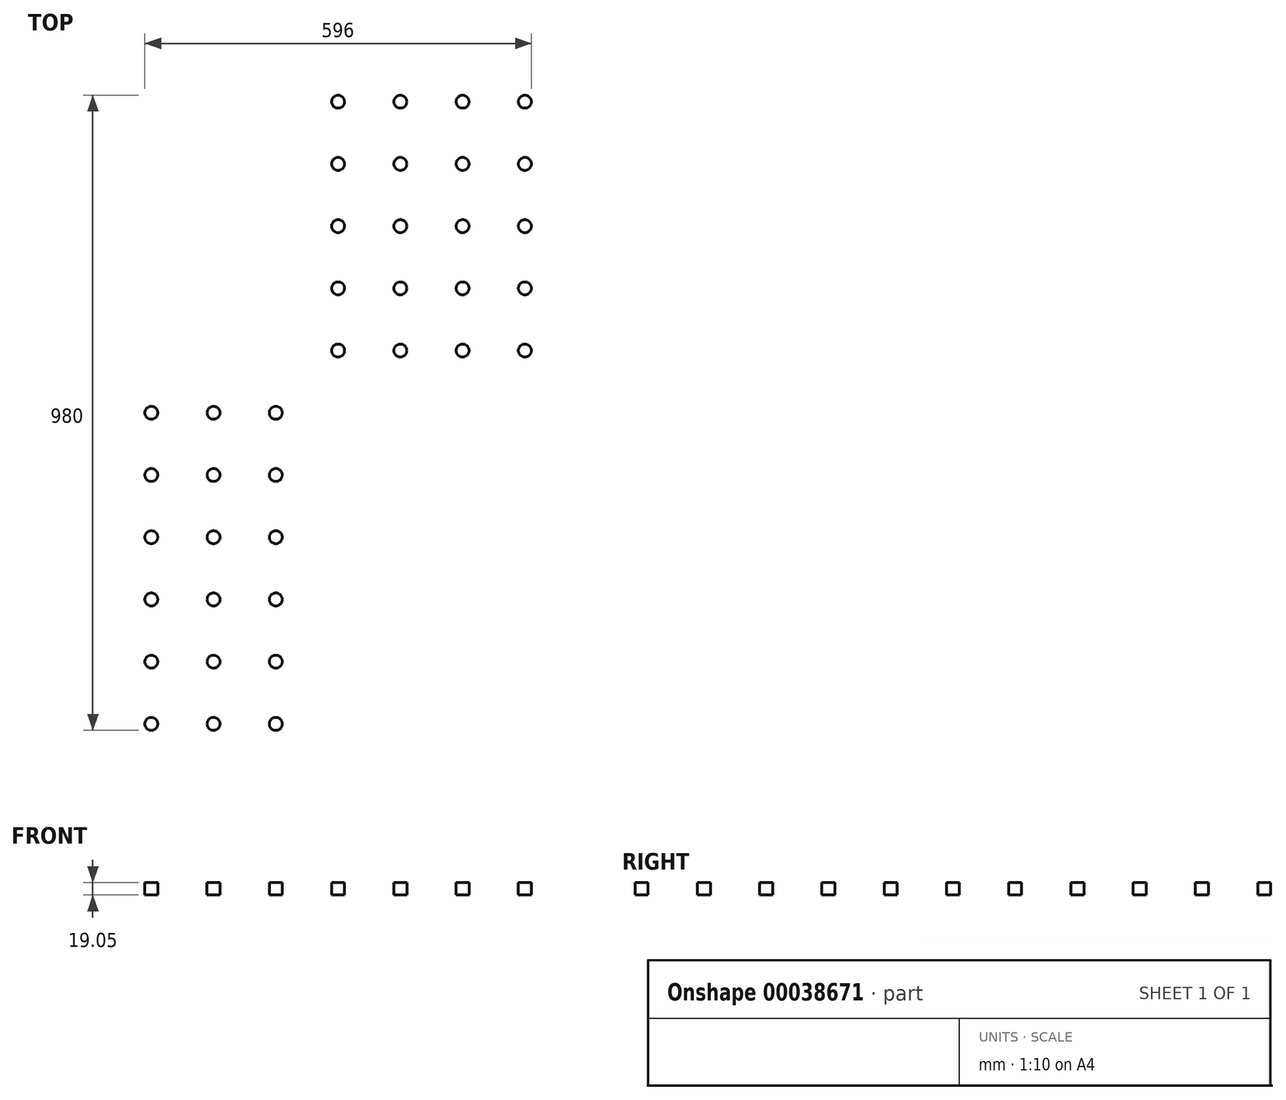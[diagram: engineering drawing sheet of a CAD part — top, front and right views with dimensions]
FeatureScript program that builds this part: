
annotation { "Feature Type Name" : "Feature", "Feature Type Description" : "" }
export const myFeature = defineFeature(function(context is Context, id is Id, definition is map)
    precondition{}
    {
        {
            var Q0;
            Q0=qCreatedBy(makeId("Top.planeOp"),FACE);
            var sketch = newSketch(context, id + "F0", { "sketchPlane" : qUnion([Q0])});
            skLineSegment(sketch, "E0.bottom", {"start": v(0, 0) * mm, "end": v(718, 0) * mm});
            skLineSegment(sketch, "E0.top", {"start": v(0, -1102) * mm, "end": v(718, -1102) * mm});
            skLineSegment(sketch, "E0.left", {"start": v(0, 0) * mm, "end": v(0, -1102) * mm});
            skLineSegment(sketch, "E0.right", {"start": v(718, 0) * mm, "end": v(718, -1102) * mm});
            skSolve(sketch);
        }
        {
            var Q0;
            Q0=makeQuery(id+"F0.imprint","IMPRINT",FACE,{"disambiguationData":[TD([[makeQuery(id+"F0.imprint","IMPRINT",EDGE,{"derivedFrom":sQuery(id+"F0.wireOp",EDGE,"E0.bottom")}),-1.0]])]});
            extrude(context, id + "F1", {"entities" : qUnion([Q0]), "oppositeDirection" : true, "depth" : 19.05 * mm});
        }
        {
            var Q0;
            Q0=makeQuery(id+"F1.opExtrude","CAP_FACE",FACE,{"disambiguationData":[OSD([sQuery(id+"F0.wireOp",EDGE,"E0.bottom"),sQuery(id+"F0.wireOp",EDGE,"E0.top"),sQuery(id+"F0.wireOp",EDGE,"E0.left"),sQuery(id+"F0.wireOp",EDGE,"E0.right")])],"isStart":false});
            var sketch = newSketch(context, id + "F2", { "sketchPlane" : qUnion([Q0])});
            skLineSegment(sketch, "E1", {"start": v(0, 551) * mm, "end": v(718, 551) * mm, "construction": true});
            skLineSegment(sketch, "E2", {"start": v(359, 1102) * mm, "end": v(359, 0) * mm, "construction": true});
            skCircle(sketch, "E3", {"center": v(359, 551) * mm, "radius": 10 * mm});
            skCircle(sketch, "E4.0.1.0", {"center": v(359, 647) * mm, "radius": 10 * mm});
            skCircle(sketch, "E4.0.2.0", {"center": v(359, 743) * mm, "radius": 10 * mm});
            skCircle(sketch, "E4.0.3.0", {"center": v(359, 839) * mm, "radius": 10 * mm});
            skCircle(sketch, "E4.0.4.0", {"center": v(359, 935) * mm, "radius": 10 * mm});
            skCircle(sketch, "E4.0.5.0", {"center": v(359, 1031) * mm, "radius": 10 * mm});
            skCircle(sketch, "E4.1.0.0", {"center": v(455, 551) * mm, "radius": 10 * mm});
            skCircle(sketch, "E4.1.1.0", {"center": v(455, 647) * mm, "radius": 10 * mm});
            skCircle(sketch, "E4.1.2.0", {"center": v(455, 743) * mm, "radius": 10 * mm});
            skCircle(sketch, "E4.1.3.0", {"center": v(455, 839) * mm, "radius": 10 * mm});
            skCircle(sketch, "E4.1.4.0", {"center": v(455, 935) * mm, "radius": 10 * mm});
            skCircle(sketch, "E4.1.5.0", {"center": v(455, 1031) * mm, "radius": 10 * mm});
            skCircle(sketch, "E4.2.0.0", {"center": v(551, 551) * mm, "radius": 10 * mm});
            skCircle(sketch, "E4.2.1.0", {"center": v(551, 647) * mm, "radius": 10 * mm});
            skCircle(sketch, "E4.2.2.0", {"center": v(551, 743) * mm, "radius": 10 * mm});
            skCircle(sketch, "E4.2.3.0", {"center": v(551, 839) * mm, "radius": 10 * mm});
            skCircle(sketch, "E4.2.4.0", {"center": v(551, 935) * mm, "radius": 10 * mm});
            skCircle(sketch, "E4.2.5.0", {"center": v(551, 1031) * mm, "radius": 10 * mm});
            skCircle(sketch, "E4.3.0.0", {"center": v(647, 551) * mm, "radius": 10 * mm});
            skCircle(sketch, "E4.3.1.0", {"center": v(647, 647) * mm, "radius": 10 * mm});
            skCircle(sketch, "E4.3.2.0", {"center": v(647, 743) * mm, "radius": 10 * mm});
            skCircle(sketch, "E4.3.3.0", {"center": v(647, 839) * mm, "radius": 10 * mm});
            skCircle(sketch, "E4.3.4.0", {"center": v(647, 935) * mm, "radius": 10 * mm});
            skCircle(sketch, "E4.3.5.0", {"center": v(647, 1031) * mm, "radius": 10 * mm});
            skLineSegment(sketch, "E4.direction1", {"start": v(359, 551) * mm, "end": v(455, 551) * mm, "construction": true});
            skLineSegment(sketch, "E4.direction2", {"start": v(359, 551) * mm, "end": v(359, 647) * mm, "construction": true});
            skCircle(sketch, "E5.MirrorC", {"center": v(263, 551) * mm, "radius": 10 * mm});
            skCircle(sketch, "E6.MirrorC", {"center": v(263, 839) * mm, "radius": 10 * mm});
            skCircle(sketch, "E7.MirrorC", {"center": v(167, 551) * mm, "radius": 10 * mm});
            skCircle(sketch, "E8.MirrorC", {"center": v(71, 1031) * mm, "radius": 10 * mm});
            skCircle(sketch, "E9.MirrorC", {"center": v(71, 839) * mm, "radius": 10 * mm});
            skCircle(sketch, "E10.MirrorC", {"center": v(71, 743) * mm, "radius": 10 * mm});
            skCircle(sketch, "E11.MirrorC", {"center": v(71, 935) * mm, "radius": 10 * mm});
            skCircle(sketch, "E12.MirrorC", {"center": v(71, 647) * mm, "radius": 10 * mm});
            skCircle(sketch, "E13.MirrorC", {"center": v(167, 839) * mm, "radius": 10 * mm});
            skCircle(sketch, "E14.MirrorC", {"center": v(167, 935) * mm, "radius": 10 * mm});
            skCircle(sketch, "E15.MirrorC", {"center": v(167, 1031) * mm, "radius": 10 * mm});
            skCircle(sketch, "E16.MirrorC", {"center": v(167, 647) * mm, "radius": 10 * mm});
            skCircle(sketch, "E17.MirrorC", {"center": v(71, 551) * mm, "radius": 10 * mm});
            skCircle(sketch, "E18.MirrorC", {"center": v(167, 743) * mm, "radius": 10 * mm});
            skCircle(sketch, "E19.MirrorC", {"center": v(263, 935) * mm, "radius": 10 * mm});
            skCircle(sketch, "E20.MirrorC", {"center": v(263, 647) * mm, "radius": 10 * mm});
            skCircle(sketch, "E21.MirrorC", {"center": v(263, 1031) * mm, "radius": 10 * mm});
            skCircle(sketch, "E22.MirrorC", {"center": v(263, 743) * mm, "radius": 10 * mm});
            skCircle(sketch, "E23.MirrorC", {"center": v(263, 359) * mm, "radius": 10 * mm});
            skCircle(sketch, "E24.MirrorC", {"center": v(359, 455) * mm, "radius": 10 * mm});
            skCircle(sketch, "E25.MirrorC", {"center": v(551, 71) * mm, "radius": 10 * mm});
            skCircle(sketch, "E26.MirrorC", {"center": v(455, 455) * mm, "radius": 10 * mm});
            skCircle(sketch, "E27.MirrorC", {"center": v(359, 263) * mm, "radius": 10 * mm});
            skCircle(sketch, "E28.MirrorC", {"center": v(359, 359) * mm, "radius": 10 * mm});
            skCircle(sketch, "E29.MirrorC", {"center": v(551, 359) * mm, "radius": 10 * mm});
            skCircle(sketch, "E30.MirrorC", {"center": v(71, 263) * mm, "radius": 10 * mm});
            skCircle(sketch, "E31.MirrorC", {"center": v(551, 263) * mm, "radius": 10 * mm});
            skCircle(sketch, "E32.MirrorC", {"center": v(167, 263) * mm, "radius": 10 * mm});
            skCircle(sketch, "E33.MirrorC", {"center": v(263, 263) * mm, "radius": 10 * mm});
            skCircle(sketch, "E34.MirrorC", {"center": v(647, 263) * mm, "radius": 10 * mm});
            skCircle(sketch, "E35.MirrorC", {"center": v(167, 455) * mm, "radius": 10 * mm});
            skCircle(sketch, "E36.MirrorC", {"center": v(263, 455) * mm, "radius": 10 * mm});
            skCircle(sketch, "E37.MirrorC", {"center": v(455, 359) * mm, "radius": 10 * mm});
            skCircle(sketch, "E38.MirrorC", {"center": v(455, 263) * mm, "radius": 10 * mm});
            skCircle(sketch, "E39.MirrorC", {"center": v(71, 359) * mm, "radius": 10 * mm});
            skCircle(sketch, "E40.MirrorC", {"center": v(455, 71) * mm, "radius": 10 * mm});
            skCircle(sketch, "E41.MirrorC", {"center": v(647, 359) * mm, "radius": 10 * mm});
            skCircle(sketch, "E42.MirrorC", {"center": v(167, 71) * mm, "radius": 10 * mm});
            skCircle(sketch, "E43.MirrorC", {"center": v(359, 71) * mm, "radius": 10 * mm});
            skCircle(sketch, "E44.MirrorC", {"center": v(71, 71) * mm, "radius": 10 * mm});
            skCircle(sketch, "E45.MirrorC", {"center": v(359, 167) * mm, "radius": 10 * mm});
            skCircle(sketch, "E46.MirrorC", {"center": v(167, 167) * mm, "radius": 10 * mm});
            skCircle(sketch, "E47.MirrorC", {"center": v(263, 71) * mm, "radius": 10 * mm});
            skCircle(sketch, "E48.MirrorC", {"center": v(71, 455) * mm, "radius": 10 * mm});
            skCircle(sketch, "E49.MirrorC", {"center": v(551, 167) * mm, "radius": 10 * mm});
            skCircle(sketch, "E50.MirrorC", {"center": v(167, 359) * mm, "radius": 10 * mm});
            skCircle(sketch, "E51.MirrorC", {"center": v(647, 71) * mm, "radius": 10 * mm});
            skCircle(sketch, "E52.MirrorC", {"center": v(551, 455) * mm, "radius": 10 * mm});
            skCircle(sketch, "E53.MirrorC", {"center": v(647, 167) * mm, "radius": 10 * mm});
            skCircle(sketch, "E54.MirrorC", {"center": v(455, 167) * mm, "radius": 10 * mm});
            skCircle(sketch, "E55.MirrorC", {"center": v(263, 167) * mm, "radius": 10 * mm});
            skCircle(sketch, "E56.MirrorC", {"center": v(647, 455) * mm, "radius": 10 * mm});
            skCircle(sketch, "E57.MirrorC", {"center": v(71, 167) * mm, "radius": 10 * mm});
            skSolve(sketch);
        }
        {
            var Q0;
            Q0=makeQuery(id+"F2.imprint","IMPRINT",FACE,{"disambiguationData":[TD([[makeQuery(id+"F2.imprint","IMPRINT",EDGE,{"derivedFrom":sQuery(id+"F2.wireOp",EDGE,"E3")}),1.0]])]});
            var Q1;
            Q1=makeQuery(id+"F2.imprint","IMPRINT",FACE,{"disambiguationData":[TD([[makeQuery(id+"F2.imprint","IMPRINT",EDGE,{"derivedFrom":sQuery(id+"F2.wireOp",EDGE,"E5.MirrorC")}),-1.0]])]});
            var Q2;
            Q2=makeQuery(id+"F2.imprint","IMPRINT",FACE,{"disambiguationData":[TD([[makeQuery(id+"F2.imprint","IMPRINT",EDGE,{"derivedFrom":sQuery(id+"F2.wireOp",EDGE,"E4.3.4.0")}),1.0]])]});
            var Q3;
            Q3=makeQuery(id+"F2.imprint","IMPRINT",FACE,{"disambiguationData":[TD([[makeQuery(id+"F2.imprint","IMPRINT",EDGE,{"derivedFrom":sQuery(id+"F2.wireOp",EDGE,"E19.MirrorC")}),-1.0]])]});
            var Q4;
            Q4=makeQuery(id+"F2.imprint","IMPRINT",FACE,{"disambiguationData":[TD([[makeQuery(id+"F2.imprint","IMPRINT",EDGE,{"derivedFrom":sQuery(id+"F2.wireOp",EDGE,"E27.MirrorC")}),-1.0]])]});
            var Q5;
            Q5=makeQuery(id+"F2.imprint","IMPRINT",FACE,{"disambiguationData":[TD([[makeQuery(id+"F2.imprint","IMPRINT",EDGE,{"derivedFrom":sQuery(id+"F2.wireOp",EDGE,"E30.MirrorC")}),1.0]])]});
            var Q6;
            Q6=makeQuery(id+"F2.imprint","IMPRINT",FACE,{"disambiguationData":[TD([[makeQuery(id+"F2.imprint","IMPRINT",EDGE,{"derivedFrom":sQuery(id+"F2.wireOp",EDGE,"E4.2.5.0")}),1.0]])]});
            var Q7;
            Q7=makeQuery(id+"F2.imprint","IMPRINT",FACE,{"disambiguationData":[TD([[makeQuery(id+"F2.imprint","IMPRINT",EDGE,{"derivedFrom":sQuery(id+"F2.wireOp",EDGE,"E53.MirrorC")}),-1.0]])]});
            var Q8;
            Q8=makeQuery(id+"F2.imprint","IMPRINT",FACE,{"disambiguationData":[TD([[makeQuery(id+"F2.imprint","IMPRINT",EDGE,{"derivedFrom":sQuery(id+"F2.wireOp",EDGE,"E22.MirrorC")}),-1.0]])]});
            var Q9;
            Q9=makeQuery(id+"F2.imprint","IMPRINT",FACE,{"disambiguationData":[TD([[makeQuery(id+"F2.imprint","IMPRINT",EDGE,{"derivedFrom":sQuery(id+"F2.wireOp",EDGE,"E44.MirrorC")}),1.0]])]});
            var Q10;
            Q10=makeQuery(id+"F2.imprint","IMPRINT",FACE,{"disambiguationData":[TD([[makeQuery(id+"F2.imprint","IMPRINT",EDGE,{"derivedFrom":sQuery(id+"F2.wireOp",EDGE,"E37.MirrorC")}),-1.0]])]});
            var Q11;
            Q11=makeQuery(id+"F2.imprint","IMPRINT",FACE,{"disambiguationData":[TD([[makeQuery(id+"F2.imprint","IMPRINT",EDGE,{"derivedFrom":sQuery(id+"F2.wireOp",EDGE,"E34.MirrorC")}),-1.0]])]});
            var Q12;
            Q12=makeQuery(id+"F2.imprint","IMPRINT",FACE,{"disambiguationData":[TD([[makeQuery(id+"F2.imprint","IMPRINT",EDGE,{"derivedFrom":sQuery(id+"F2.wireOp",EDGE,"E6.MirrorC")}),-1.0]])]});
            var Q13;
            Q13=makeQuery(id+"F2.imprint","IMPRINT",FACE,{"disambiguationData":[TD([[makeQuery(id+"F2.imprint","IMPRINT",EDGE,{"derivedFrom":sQuery(id+"F2.wireOp",EDGE,"E43.MirrorC")}),-1.0]])]});
            var Q14;
            Q14=makeQuery(id+"F2.imprint","IMPRINT",FACE,{"disambiguationData":[TD([[makeQuery(id+"F2.imprint","IMPRINT",EDGE,{"derivedFrom":sQuery(id+"F2.wireOp",EDGE,"E39.MirrorC")}),1.0]])]});
            var Q15;
            Q15=makeQuery(id+"F2.imprint","IMPRINT",FACE,{"disambiguationData":[TD([[makeQuery(id+"F2.imprint","IMPRINT",EDGE,{"derivedFrom":sQuery(id+"F2.wireOp",EDGE,"E55.MirrorC")}),1.0]])]});
            var Q16;
            Q16=makeQuery(id+"F2.imprint","IMPRINT",FACE,{"disambiguationData":[TD([[makeQuery(id+"F2.imprint","IMPRINT",EDGE,{"derivedFrom":sQuery(id+"F2.wireOp",EDGE,"E56.MirrorC")}),-1.0]])]});
            var Q17;
            Q17=makeQuery(id+"F2.imprint","IMPRINT",FACE,{"disambiguationData":[TD([[makeQuery(id+"F2.imprint","IMPRINT",EDGE,{"derivedFrom":sQuery(id+"F2.wireOp",EDGE,"E40.MirrorC")}),-1.0]])]});
            var Q18;
            Q18=makeQuery(id+"F2.imprint","IMPRINT",FACE,{"disambiguationData":[TD([[makeQuery(id+"F2.imprint","IMPRINT",EDGE,{"derivedFrom":sQuery(id+"F2.wireOp",EDGE,"E4.1.5.0")}),1.0]])]});
            var Q19;
            Q19=makeQuery(id+"F2.imprint","IMPRINT",FACE,{"disambiguationData":[TD([[makeQuery(id+"F2.imprint","IMPRINT",EDGE,{"derivedFrom":sQuery(id+"F2.wireOp",EDGE,"E54.MirrorC")}),-1.0]])]});
            var Q20;
            Q20=makeQuery(id+"F2.imprint","IMPRINT",FACE,{"disambiguationData":[TD([[makeQuery(id+"F2.imprint","IMPRINT",EDGE,{"derivedFrom":sQuery(id+"F2.wireOp",EDGE,"E28.MirrorC")}),-1.0]])]});
            var Q21;
            Q21=makeQuery(id+"F2.imprint","IMPRINT",FACE,{"disambiguationData":[TD([[makeQuery(id+"F2.imprint","IMPRINT",EDGE,{"derivedFrom":sQuery(id+"F2.wireOp",EDGE,"E32.MirrorC")}),1.0]])]});
            var Q22;
            Q22=makeQuery(id+"F2.imprint","IMPRINT",FACE,{"disambiguationData":[TD([[makeQuery(id+"F2.imprint","IMPRINT",EDGE,{"derivedFrom":sQuery(id+"F2.wireOp",EDGE,"E50.MirrorC")}),1.0]])]});
            var Q23;
            Q23=makeQuery(id+"F2.imprint","IMPRINT",FACE,{"disambiguationData":[TD([[makeQuery(id+"F2.imprint","IMPRINT",EDGE,{"derivedFrom":sQuery(id+"F2.wireOp",EDGE,"E12.MirrorC")}),-1.0]])]});
            var Q24;
            Q24=makeQuery(id+"F2.imprint","IMPRINT",FACE,{"disambiguationData":[TD([[makeQuery(id+"F2.imprint","IMPRINT",EDGE,{"derivedFrom":sQuery(id+"F2.wireOp",EDGE,"E24.MirrorC")}),-1.0]])]});
            var Q25;
            Q25=makeQuery(id+"F2.imprint","IMPRINT",FACE,{"disambiguationData":[TD([[makeQuery(id+"F2.imprint","IMPRINT",EDGE,{"derivedFrom":sQuery(id+"F2.wireOp",EDGE,"E4.2.3.0")}),1.0]])]});
            var Q26;
            Q26=makeQuery(id+"F2.imprint","IMPRINT",FACE,{"disambiguationData":[TD([[makeQuery(id+"F2.imprint","IMPRINT",EDGE,{"derivedFrom":sQuery(id+"F2.wireOp",EDGE,"E38.MirrorC")}),-1.0]])]});
            var Q27;
            Q27=makeQuery(id+"F2.imprint","IMPRINT",FACE,{"disambiguationData":[TD([[makeQuery(id+"F2.imprint","IMPRINT",EDGE,{"derivedFrom":sQuery(id+"F2.wireOp",EDGE,"E4.3.3.0")}),1.0]])]});
            var Q28;
            Q28=makeQuery(id+"F2.imprint","IMPRINT",FACE,{"disambiguationData":[TD([[makeQuery(id+"F2.imprint","IMPRINT",EDGE,{"derivedFrom":sQuery(id+"F2.wireOp",EDGE,"E14.MirrorC")}),-1.0]])]});
            var Q29;
            Q29=makeQuery(id+"F2.imprint","IMPRINT",FACE,{"disambiguationData":[TD([[makeQuery(id+"F2.imprint","IMPRINT",EDGE,{"derivedFrom":sQuery(id+"F2.wireOp",EDGE,"E21.MirrorC")}),-1.0]])]});
            var Q30;
            Q30=makeQuery(id+"F2.imprint","IMPRINT",FACE,{"disambiguationData":[TD([[makeQuery(id+"F2.imprint","IMPRINT",EDGE,{"derivedFrom":sQuery(id+"F2.wireOp",EDGE,"E35.MirrorC")}),1.0]])]});
            var Q31;
            Q31=makeQuery(id+"F2.imprint","IMPRINT",FACE,{"disambiguationData":[TD([[makeQuery(id+"F2.imprint","IMPRINT",EDGE,{"derivedFrom":sQuery(id+"F2.wireOp",EDGE,"E4.2.1.0")}),1.0]])]});
            var Q32;
            Q32=makeQuery(id+"F2.imprint","IMPRINT",FACE,{"disambiguationData":[TD([[makeQuery(id+"F2.imprint","IMPRINT",EDGE,{"derivedFrom":sQuery(id+"F2.wireOp",EDGE,"E23.MirrorC")}),1.0]])]});
            var Q33;
            Q33=makeQuery(id+"F2.imprint","IMPRINT",FACE,{"disambiguationData":[TD([[makeQuery(id+"F2.imprint","IMPRINT",EDGE,{"derivedFrom":sQuery(id+"F2.wireOp",EDGE,"E7.MirrorC")}),-1.0]])]});
            var Q34;
            Q34=makeQuery(id+"F2.imprint","IMPRINT",FACE,{"disambiguationData":[TD([[makeQuery(id+"F2.imprint","IMPRINT",EDGE,{"derivedFrom":sQuery(id+"F2.wireOp",EDGE,"E4.2.2.0")}),1.0]])]});
            var Q35;
            Q35=makeQuery(id+"F2.imprint","IMPRINT",FACE,{"disambiguationData":[TD([[makeQuery(id+"F2.imprint","IMPRINT",EDGE,{"derivedFrom":sQuery(id+"F2.wireOp",EDGE,"E4.3.0.0")}),1.0]])]});
            var Q36;
            Q36=makeQuery(id+"F2.imprint","IMPRINT",FACE,{"disambiguationData":[TD([[makeQuery(id+"F2.imprint","IMPRINT",EDGE,{"derivedFrom":sQuery(id+"F2.wireOp",EDGE,"E4.0.5.0")}),1.0]])]});
            var Q37;
            Q37=makeQuery(id+"F2.imprint","IMPRINT",FACE,{"disambiguationData":[TD([[makeQuery(id+"F2.imprint","IMPRINT",EDGE,{"derivedFrom":sQuery(id+"F2.wireOp",EDGE,"E10.MirrorC")}),-1.0]])]});
            var Q38;
            Q38=makeQuery(id+"F2.imprint","IMPRINT",FACE,{"disambiguationData":[TD([[makeQuery(id+"F2.imprint","IMPRINT",EDGE,{"derivedFrom":sQuery(id+"F2.wireOp",EDGE,"E17.MirrorC")}),-1.0]])]});
            var Q39;
            Q39=makeQuery(id+"F2.imprint","IMPRINT",FACE,{"disambiguationData":[TD([[makeQuery(id+"F2.imprint","IMPRINT",EDGE,{"derivedFrom":sQuery(id+"F2.wireOp",EDGE,"E4.3.2.0")}),1.0]])]});
            var Q40;
            Q40=makeQuery(id+"F2.imprint","IMPRINT",FACE,{"disambiguationData":[TD([[makeQuery(id+"F2.imprint","IMPRINT",EDGE,{"derivedFrom":sQuery(id+"F2.wireOp",EDGE,"E9.MirrorC")}),-1.0]])]});
            var Q41;
            Q41=makeQuery(id+"F2.imprint","IMPRINT",FACE,{"disambiguationData":[TD([[makeQuery(id+"F2.imprint","IMPRINT",EDGE,{"derivedFrom":sQuery(id+"F2.wireOp",EDGE,"E25.MirrorC")}),-1.0]])]});
            var Q42;
            Q42=makeQuery(id+"F2.imprint","IMPRINT",FACE,{"disambiguationData":[TD([[makeQuery(id+"F2.imprint","IMPRINT",EDGE,{"derivedFrom":sQuery(id+"F2.wireOp",EDGE,"E51.MirrorC")}),-1.0]])]});
            var Q43;
            Q43=makeQuery(id+"F2.imprint","IMPRINT",FACE,{"disambiguationData":[TD([[makeQuery(id+"F2.imprint","IMPRINT",EDGE,{"derivedFrom":sQuery(id+"F2.wireOp",EDGE,"E45.MirrorC")}),-1.0]])]});
            var Q44;
            Q44=makeQuery(id+"F2.imprint","IMPRINT",FACE,{"disambiguationData":[TD([[makeQuery(id+"F2.imprint","IMPRINT",EDGE,{"derivedFrom":sQuery(id+"F2.wireOp",EDGE,"E46.MirrorC")}),1.0]])]});
            var Q45;
            Q45=makeQuery(id+"F2.imprint","IMPRINT",FACE,{"disambiguationData":[TD([[makeQuery(id+"F2.imprint","IMPRINT",EDGE,{"derivedFrom":sQuery(id+"F2.wireOp",EDGE,"E16.MirrorC")}),-1.0]])]});
            var Q46;
            Q46=makeQuery(id+"F2.imprint","IMPRINT",FACE,{"disambiguationData":[TD([[makeQuery(id+"F2.imprint","IMPRINT",EDGE,{"derivedFrom":sQuery(id+"F2.wireOp",EDGE,"E13.MirrorC")}),-1.0]])]});
            var Q47;
            Q47=makeQuery(id+"F2.imprint","IMPRINT",FACE,{"disambiguationData":[TD([[makeQuery(id+"F2.imprint","IMPRINT",EDGE,{"derivedFrom":sQuery(id+"F2.wireOp",EDGE,"E57.MirrorC")}),1.0]])]});
            var Q48;
            Q48=makeQuery(id+"F2.imprint","IMPRINT",FACE,{"disambiguationData":[TD([[makeQuery(id+"F2.imprint","IMPRINT",EDGE,{"derivedFrom":sQuery(id+"F2.wireOp",EDGE,"E41.MirrorC")}),-1.0]])]});
            var Q49;
            Q49=makeQuery(id+"F2.imprint","IMPRINT",FACE,{"disambiguationData":[TD([[makeQuery(id+"F2.imprint","IMPRINT",EDGE,{"derivedFrom":sQuery(id+"F2.wireOp",EDGE,"E47.MirrorC")}),1.0]])]});
            var Q50;
            Q50=makeQuery(id+"F2.imprint","IMPRINT",FACE,{"disambiguationData":[TD([[makeQuery(id+"F2.imprint","IMPRINT",EDGE,{"derivedFrom":sQuery(id+"F2.wireOp",EDGE,"E4.3.5.0")}),1.0]])]});
            var Q51;
            Q51=makeQuery(id+"F2.imprint","IMPRINT",FACE,{"disambiguationData":[TD([[makeQuery(id+"F2.imprint","IMPRINT",EDGE,{"derivedFrom":sQuery(id+"F2.wireOp",EDGE,"E20.MirrorC")}),-1.0]])]});
            var Q52;
            Q52=makeQuery(id+"F2.imprint","IMPRINT",FACE,{"disambiguationData":[TD([[makeQuery(id+"F2.imprint","IMPRINT",EDGE,{"derivedFrom":sQuery(id+"F2.wireOp",EDGE,"E36.MirrorC")}),1.0]])]});
            var Q53;
            Q53=makeQuery(id+"F2.imprint","IMPRINT",FACE,{"disambiguationData":[TD([[makeQuery(id+"F2.imprint","IMPRINT",EDGE,{"derivedFrom":sQuery(id+"F2.wireOp",EDGE,"E52.MirrorC")}),-1.0]])]});
            var Q54;
            Q54=makeQuery(id+"F2.imprint","IMPRINT",FACE,{"disambiguationData":[TD([[makeQuery(id+"F2.imprint","IMPRINT",EDGE,{"derivedFrom":sQuery(id+"F2.wireOp",EDGE,"E29.MirrorC")}),-1.0]])]});
            var Q55;
            Q55=makeQuery(id+"F2.imprint","IMPRINT",FACE,{"disambiguationData":[TD([[makeQuery(id+"F2.imprint","IMPRINT",EDGE,{"derivedFrom":sQuery(id+"F2.wireOp",EDGE,"E11.MirrorC")}),-1.0]])]});
            var Q56;
            Q56=makeQuery(id+"F2.imprint","IMPRINT",FACE,{"disambiguationData":[TD([[makeQuery(id+"F2.imprint","IMPRINT",EDGE,{"derivedFrom":sQuery(id+"F2.wireOp",EDGE,"E48.MirrorC")}),1.0]])]});
            var Q57;
            Q57=makeQuery(id+"F2.imprint","IMPRINT",FACE,{"disambiguationData":[TD([[makeQuery(id+"F2.imprint","IMPRINT",EDGE,{"derivedFrom":sQuery(id+"F2.wireOp",EDGE,"E4.1.4.0")}),1.0]])]});
            var Q58;
            Q58=makeQuery(id+"F2.imprint","IMPRINT",FACE,{"disambiguationData":[TD([[makeQuery(id+"F2.imprint","IMPRINT",EDGE,{"derivedFrom":sQuery(id+"F2.wireOp",EDGE,"E4.2.4.0")}),1.0]])]});
            var Q59;
            Q59=makeQuery(id+"F2.imprint","IMPRINT",FACE,{"disambiguationData":[TD([[makeQuery(id+"F2.imprint","IMPRINT",EDGE,{"derivedFrom":sQuery(id+"F2.wireOp",EDGE,"E31.MirrorC")}),-1.0]])]});
            var Q60;
            Q60=makeQuery(id+"F2.imprint","IMPRINT",FACE,{"disambiguationData":[TD([[makeQuery(id+"F2.imprint","IMPRINT",EDGE,{"derivedFrom":sQuery(id+"F2.wireOp",EDGE,"E8.MirrorC")}),-1.0]])]});
            var Q61;
            Q61=makeQuery(id+"F2.imprint","IMPRINT",FACE,{"disambiguationData":[TD([[makeQuery(id+"F2.imprint","IMPRINT",EDGE,{"derivedFrom":sQuery(id+"F2.wireOp",EDGE,"E4.0.4.0")}),1.0]])]});
            var Q62;
            Q62=makeQuery(id+"F2.imprint","IMPRINT",FACE,{"disambiguationData":[TD([[makeQuery(id+"F2.imprint","IMPRINT",EDGE,{"derivedFrom":sQuery(id+"F2.wireOp",EDGE,"E4.1.3.0")}),1.0]])]});
            var Q63;
            Q63=makeQuery(id+"F2.imprint","IMPRINT",FACE,{"disambiguationData":[TD([[makeQuery(id+"F2.imprint","IMPRINT",EDGE,{"derivedFrom":sQuery(id+"F2.wireOp",EDGE,"E4.2.0.0")}),1.0]])]});
            var Q64;
            Q64=makeQuery(id+"F2.imprint","IMPRINT",FACE,{"disambiguationData":[TD([[makeQuery(id+"F2.imprint","IMPRINT",EDGE,{"derivedFrom":sQuery(id+"F2.wireOp",EDGE,"E4.0.1.0")}),1.0]])]});
            var Q65;
            Q65=makeQuery(id+"F2.imprint","IMPRINT",FACE,{"disambiguationData":[TD([[makeQuery(id+"F2.imprint","IMPRINT",EDGE,{"derivedFrom":sQuery(id+"F2.wireOp",EDGE,"E4.1.2.0")}),1.0]])]});
            var Q66;
            Q66=makeQuery(id+"F2.imprint","IMPRINT",FACE,{"disambiguationData":[TD([[makeQuery(id+"F2.imprint","IMPRINT",EDGE,{"derivedFrom":sQuery(id+"F2.wireOp",EDGE,"E4.1.1.0")}),1.0]])]});
            var Q67;
            Q67=makeQuery(id+"F2.imprint","IMPRINT",FACE,{"disambiguationData":[TD([[makeQuery(id+"F2.imprint","IMPRINT",EDGE,{"derivedFrom":sQuery(id+"F2.wireOp",EDGE,"E4.1.0.0")}),1.0]])]});
            var Q68;
            Q68=makeQuery(id+"F2.imprint","IMPRINT",FACE,{"disambiguationData":[TD([[makeQuery(id+"F2.imprint","IMPRINT",EDGE,{"derivedFrom":sQuery(id+"F2.wireOp",EDGE,"E4.0.3.0")}),1.0]])]});
            var Q69;
            Q69=makeQuery(id+"F2.imprint","IMPRINT",FACE,{"disambiguationData":[TD([[makeQuery(id+"F2.imprint","IMPRINT",EDGE,{"derivedFrom":sQuery(id+"F2.wireOp",EDGE,"E15.MirrorC")}),-1.0]])]});
            var Q70;
            Q70=makeQuery(id+"F2.imprint","IMPRINT",FACE,{"disambiguationData":[TD([[makeQuery(id+"F2.imprint","IMPRINT",EDGE,{"derivedFrom":sQuery(id+"F2.wireOp",EDGE,"E4.3.1.0")}),1.0]])]});
            var Q71;
            Q71=makeQuery(id+"F2.imprint","IMPRINT",FACE,{"disambiguationData":[TD([[makeQuery(id+"F2.imprint","IMPRINT",EDGE,{"derivedFrom":sQuery(id+"F2.wireOp",EDGE,"E4.0.2.0")}),1.0]])]});
            var Q72;
            Q72=makeQuery(id+"F2.imprint","IMPRINT",FACE,{"disambiguationData":[TD([[makeQuery(id+"F2.imprint","IMPRINT",EDGE,{"derivedFrom":sQuery(id+"F2.wireOp",EDGE,"E18.MirrorC")}),-1.0]])]});
            var Q73;
            Q73=makeQuery(id+"F2.imprint","IMPRINT",FACE,{"disambiguationData":[TD([[makeQuery(id+"F2.imprint","IMPRINT",EDGE,{"derivedFrom":sQuery(id+"F2.wireOp",EDGE,"E42.MirrorC")}),1.0]])]});
            var Q74;
            Q74=makeQuery(id+"F2.imprint","IMPRINT",FACE,{"disambiguationData":[TD([[makeQuery(id+"F2.imprint","IMPRINT",EDGE,{"derivedFrom":sQuery(id+"F2.wireOp",EDGE,"E49.MirrorC")}),-1.0]])]});
            var Q75;
            Q75=makeQuery(id+"F2.imprint","IMPRINT",FACE,{"disambiguationData":[TD([[makeQuery(id+"F2.imprint","IMPRINT",EDGE,{"derivedFrom":sQuery(id+"F2.wireOp",EDGE,"E33.MirrorC")}),1.0]])]});
            var Q76;
            Q76=makeQuery(id+"F2.imprint","IMPRINT",FACE,{"disambiguationData":[TD([[makeQuery(id+"F2.imprint","IMPRINT",EDGE,{"derivedFrom":sQuery(id+"F2.wireOp",EDGE,"E26.MirrorC")}),-1.0]])]});
            extrude(context, id + "F3", {"entities" : qUnion([Q0, Q1, Q2, Q3, Q4, Q5, Q6, Q7, Q8, Q9, Q10, Q11, Q12, Q13, Q14, Q15, Q16, Q17, Q18, Q19, Q20, Q21, Q22, Q23, Q24, Q25, Q26, Q27, Q28, Q29, Q30, Q31, Q32, Q33, Q34, Q35, Q36, Q37, Q38, Q39, Q40, Q41, Q42, Q43, Q44, Q45, Q46, Q47, Q48, Q49, Q50, Q51, Q52, Q53, Q54, Q55, Q56, Q57, Q58, Q59, Q60, Q61, Q62, Q63, Q64, Q65, Q66, Q67, Q68, Q69, Q70, Q71, Q72, Q73, Q74, Q75, Q76]), "operationType" : NewBodyOperationType.REMOVE, "endBound" : BoundingType.THROUGH_ALL, "oppositeDirection" : true, "depth" : 25.4 * mm});
        }
    });
